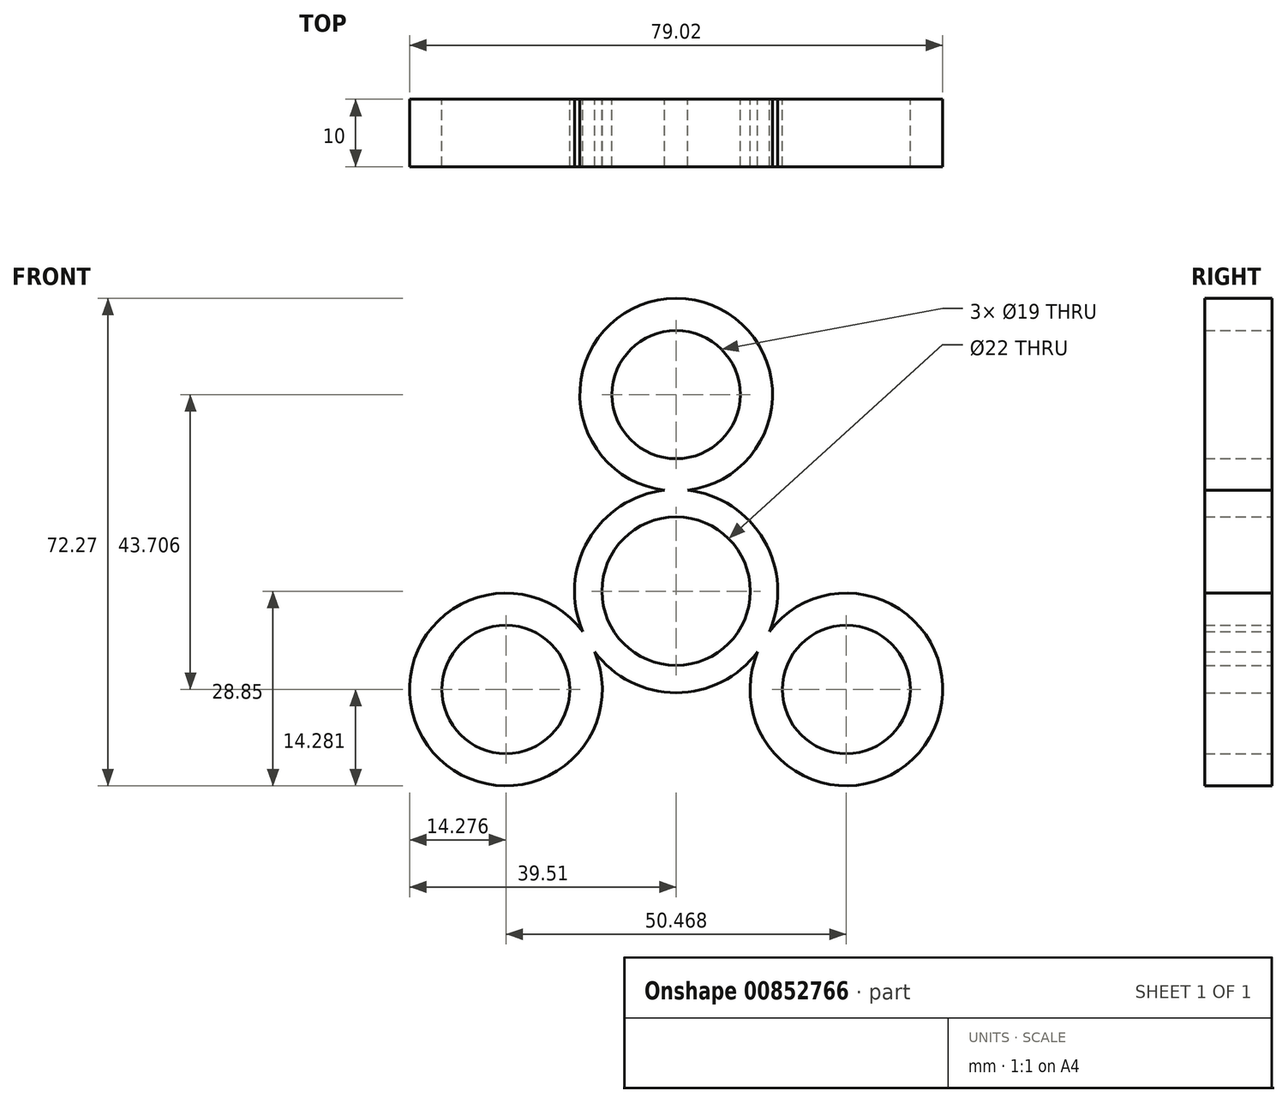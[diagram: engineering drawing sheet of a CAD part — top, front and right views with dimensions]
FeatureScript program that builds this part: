
annotation { "Feature Type Name" : "Feature", "Feature Type Description" : "" }
export const myFeature = defineFeature(function(context is Context, id is Id, definition is map)
    precondition{}
    {
        {
            var Q0;
            Q0=qCreatedBy(makeId("Front.planeOp"),FACE);
            var sketch = newSketch(context, id + "F0", { "sketchPlane" : qUnion([Q0])});
            skCircle(sketch, "E0", {"center": v(0, 0) * mm, "radius": 11 * mm});
            skCircle(sketch, "E1", {"center": v(0, 29.14) * mm, "radius": 9.5 * mm});
            skArc(sketch, "E2", {"start": v(1.73, 14.96) * mm, "mid": v(0, 43.42) * mm, "end": v(-1.73, 14.96) * mm});
            skCircle(sketch, "E3.1.0", {"center": v(-25.23, -14.57) * mm, "radius": 9.5 * mm});
            skArc(sketch, "E3.1.1", {"start": v(-13.82, -5.98) * mm, "mid": v(-37.6, -21.7) * mm, "end": v(-12.1, -8.98) * mm});
            skArc(sketch, "E3.1.3", {"start": v(-1.73, 14.96) * mm, "mid": v(-13.04, 7.53) * mm, "end": v(-13.82, -5.98) * mm});
            skCircle(sketch, "E3.2.0", {"center": v(25.23, -14.57) * mm, "radius": 9.5 * mm});
            skArc(sketch, "E3.2.1", {"start": v(12.1, -8.98) * mm, "mid": v(37.6, -21.7) * mm, "end": v(13.82, -5.98) * mm});
            skArc(sketch, "E4.trimOffspring", {"start": v(13.82, -5.98) * mm, "mid": v(13.04, 7.53) * mm, "end": v(1.73, 14.96) * mm});
            skArc(sketch, "E5.trimOffspring", {"start": v(-12.1, -8.98) * mm, "mid": v(0, -15.06) * mm, "end": v(12.1, -8.98) * mm});
            skSolve(sketch);
        }
        {
            var Q0;
            Q0=makeQuery(id+"F0.imprint","IMPRINT",FACE,{"disambiguationData":[TD([[makeQuery(id+"F0.imprint","IMPRINT",EDGE,{"derivedFrom":sQuery(id+"F0.wireOp",EDGE,"E1")}),-1.0]])]});
            extrude(context, id + "F1", {"entities" : qUnion([Q0]), "depth" : 10 * mm, "offsetDistance" : 25 * mm});
        }
    });
